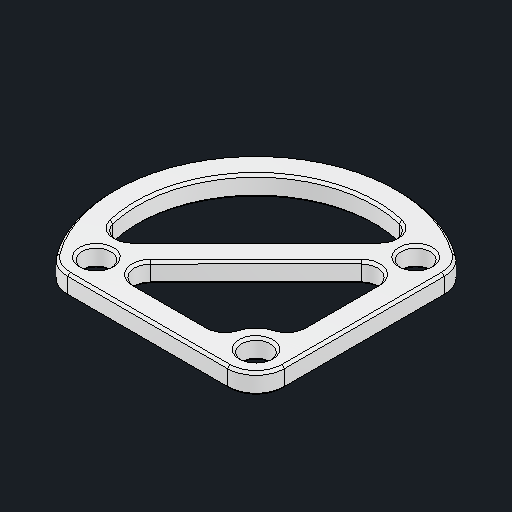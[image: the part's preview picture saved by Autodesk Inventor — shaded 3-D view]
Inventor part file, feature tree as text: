
AUTODESK INVENTOR PART (.ipt)
format: ipt  version: 2023 (Build 270158000, 158)  size: 192,512 bytes
history: native  units: in
note: dims shown in document units (in); Inventor stores cm internally (conversion verified against a paired STEP export)
features: chamfer x1
ambient origin geometry x8: Origin, YZ Plane, XZ Plane, XY Plane, X Axis, Y Axis, Z Axis, Center Point
bodies: Solid12 (feature_tree)
feature tree (1):
  chamfer  "Chamfer4"  [1 undecoded]
note: 1 required parameter value undecoded (feature->parameter linkage not recoverable at this tier; creation-order binding heuristic only, values carry confidence <= 0.55)
